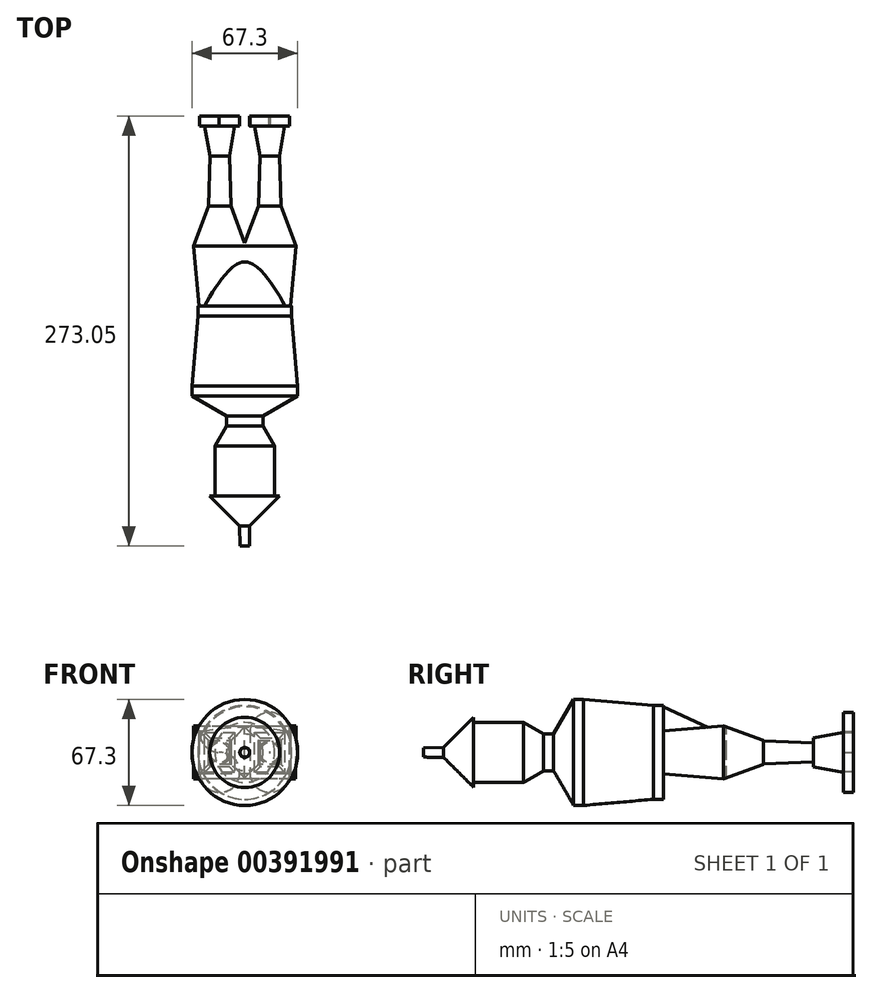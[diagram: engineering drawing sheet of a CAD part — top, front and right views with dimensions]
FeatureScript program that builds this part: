
annotation { "Feature Type Name" : "Feature", "Feature Type Description" : "" }
export const myFeature = defineFeature(function(context is Context, id is Id, definition is map)
    precondition{}
    {
        {
            var Q0;
            Q0=qCreatedBy(makeId("Front.planeOp"),FACE);
            var sketch = newSketch(context, id + "F0", { "sketchPlane" : qUnion([Q0])});
            skLineSegment(sketch, "E0", {"start": v(0, 0) * mm, "end": v(15.88, 0) * mm});
            skCircle(sketch, "E1", {"center": v(15.88, 12.7) * mm, "radius": 12.7 * mm});
            skCircle(sketch, "E2", {"center": v(15.88, -12.69) * mm, "radius": 12.7 * mm});
            skLineSegment(sketch, "E3", {"start": v(28.58, -12.69) * mm, "end": v(28.58, 12.7) * mm});
            skLineSegment(sketch, "E4", {"start": v(15.88, -12.69) * mm, "end": v(15.88, 12.7) * mm});
            skLineSegment(sketch, "E5", {"start": v(3.2, 13.5) * mm, "end": v(3.2, -11.9) * mm});
            skLineSegment(sketch, "E6", {"start": v(0, 0) * mm, "end": v(0, 9.4) * mm});
            skCircle(sketch, "E7.MirrorC", {"center": v(-15.88, -12.69) * mm, "radius": 12.7 * mm});
            skLineSegment(sketch, "E8.MirrorCS", {"start": v(-28.58, -12.69) * mm, "end": v(-28.58, 12.7) * mm});
            skCircle(sketch, "E9.MirrorC", {"center": v(-15.88, 12.7) * mm, "radius": 12.7 * mm});
            skLineSegment(sketch, "E10.MirrorCS", {"start": v(-3.2, 13.5) * mm, "end": v(-3.2, -11.9) * mm});
            skSolve(sketch);
        }
        {
            var Q0;
            {var subQ0=sQuery(id+"F0.wireOp",EDGE,"E5");var subQ1=sQuery(id+"F0.wireOp",EDGE,"E1");var subQ2=makeQuery(id+"F0.imprint","INTERSECT",VERTEX,{"disambiguationData":[OD(0.0)],"derivedFrom":[subQ1,subQ0]});Q0=makeQuery(id+"F0.imprint","IMPRINT",FACE,{"disambiguationData":[TD([[makeQuery(id+"F0.imprint","IMPRINT",EDGE,{"disambiguationData":[TD([[subQ2,-1.0]])],"derivedFrom":subQ1}),1.0]])]});}
            var Q1;
            {var subQ0=sQuery(id+"F0.wireOp",EDGE,"E10.MirrorCS");var subQ1=sQuery(id+"F0.wireOp",EDGE,"E9.MirrorC");var subQ2=makeQuery(id+"F0.imprint","INTERSECT",VERTEX,{"disambiguationData":[OD(0.0)],"derivedFrom":[subQ1,subQ0]});Q1=makeQuery(id+"F0.imprint","IMPRINT",FACE,{"disambiguationData":[TD([[makeQuery(id+"F0.imprint","IMPRINT",EDGE,{"disambiguationData":[TD([[subQ2,-1.0]])],"derivedFrom":subQ1}),-1.0]])]});}
            var Q2;
            {var subQ0=sQuery(id+"F0.wireOp",EDGE,"E5");var subQ1=sQuery(id+"F0.wireOp",EDGE,"E0");var subQ2=makeQuery(id+"F0.imprint","INTERSECT",VERTEX,{"derivedFrom":[subQ1,subQ0]});Q2=makeQuery(id+"F0.imprint","IMPRINT",FACE,{"disambiguationData":[TD([[makeQuery(id+"F0.imprint","IMPRINT",EDGE,{"disambiguationData":[TD([[subQ2,-1.0]])],"derivedFrom":subQ1}),-1.0]])]});}
            var Q3;
            {var subQ0=sQuery(id+"F0.wireOp",EDGE,"E3");Q3=makeQuery(id+"F0.imprint","IMPRINT",FACE,{"disambiguationData":[TD([[makeQuery(id+"F0.imprint","IMPRINT",EDGE,{"derivedFrom":subQ0}),1.0]])]});}
            var Q4;
            {var subQ0=sQuery(id+"F0.wireOp",EDGE,"E10.MirrorCS");var subQ1=sQuery(id+"F0.wireOp",EDGE,"E7.MirrorC");var subQ2=makeQuery(id+"F0.imprint","INTERSECT",VERTEX,{"derivedFrom":[subQ1,subQ0]});Q4=makeQuery(id+"F0.imprint","IMPRINT",FACE,{"disambiguationData":[TD([[makeQuery(id+"F0.imprint","IMPRINT",EDGE,{"disambiguationData":[TD([[subQ2,1.0]])],"derivedFrom":subQ1}),1.0]])]});}
            var Q5;
            {var subQ0=sQuery(id+"F0.wireOp",EDGE,"E5");var subQ1=sQuery(id+"F0.wireOp",EDGE,"E0");var subQ2=makeQuery(id+"F0.imprint","INTERSECT",VERTEX,{"derivedFrom":[subQ1,subQ0]});Q5=makeQuery(id+"F0.imprint","IMPRINT",FACE,{"disambiguationData":[TD([[makeQuery(id+"F0.imprint","IMPRINT",EDGE,{"disambiguationData":[TD([[subQ2,-1.0]])],"derivedFrom":subQ1}),1.0]])]});}
            var Q6;
            {var subQ0=sQuery(id+"F0.wireOp",EDGE,"E2");var subQ6=makeQuery(id+"F0.imprint","INTERSECT",VERTEX,{"derivedFrom":[subQ0,sQuery(id+"F0.wireOp",EDGE,"E3")]});Q6=makeQuery(id+"F0.imprint","IMPRINT",FACE,{"disambiguationData":[TD([[makeQuery(id+"F0.imprint","IMPRINT",EDGE,{"disambiguationData":[TD([[subQ6,-1.0]])],"derivedFrom":subQ0}),1.0]])]});}
            var Q7;
            {var subQ0=sQuery(id+"F0.wireOp",EDGE,"E9.MirrorC");var subQ2=sQuery(id+"F0.wireOp",EDGE,"E7.MirrorC");var subQ3=makeQuery(id+"F0.imprint","INTERSECT",VERTEX,{"disambiguationData":[OD(0.0)],"derivedFrom":[subQ2,subQ0]});Q7=makeQuery(id+"F0.imprint","IMPRINT",FACE,{"disambiguationData":[TD([[makeQuery(id+"F0.imprint","IMPRINT",EDGE,{"disambiguationData":[TD([[subQ3,-1.0]])],"derivedFrom":subQ2}),1.0]])]});}
            var Q8;
            {var subQ2=sQuery(id+"F0.wireOp",EDGE,"E1");var subQ7=makeQuery(id+"F0.imprint","INTERSECT",VERTEX,{"derivedFrom":[subQ2,sQuery(id+"F0.wireOp",EDGE,"E3")]});Q8=makeQuery(id+"F0.imprint","IMPRINT",FACE,{"disambiguationData":[TD([[makeQuery(id+"F0.imprint","IMPRINT",EDGE,{"disambiguationData":[TD([[subQ7,-1.0]])],"derivedFrom":subQ2}),1.0]])]});}
            var Q9;
            {var subQ0=sQuery(id+"F0.wireOp",EDGE,"E7.MirrorC");var subQ1=makeQuery(id+"F0.imprint","INTERSECT",VERTEX,{"derivedFrom":[subQ0,sQuery(id+"F0.wireOp",EDGE,"E8.MirrorCS")]});Q9=makeQuery(id+"F0.imprint","IMPRINT",FACE,{"disambiguationData":[TD([[makeQuery(id+"F0.imprint","IMPRINT",EDGE,{"disambiguationData":[TD([[subQ1,-1.0]])],"derivedFrom":subQ0}),-1.0]])]});}
            var Q10;
            {var subQ0=sQuery(id+"F0.wireOp",EDGE,"E8.MirrorCS");Q10=makeQuery(id+"F0.imprint","IMPRINT",FACE,{"disambiguationData":[TD([[makeQuery(id+"F0.imprint","IMPRINT",EDGE,{"derivedFrom":subQ0}),-1.0]])]});}
            extrude(context, id + "F1", {"entities" : qUnion([Q0, Q1, Q2, Q3, Q4, Q5, Q6, Q7, Q8, Q9, Q10]), "depth" : 6.35 * mm});
        }
        {
            var Q0;
            Q0=makeQuery(id+"F1.opExtrude","CAP_FACE",FACE,{"disambiguationData":[OSD([sQuery(id+"F0.wireOp",EDGE,"E7.MirrorC"),sQuery(id+"F0.wireOp",EDGE,"E8.MirrorCS"),sQuery(id+"F0.wireOp",EDGE,"E9.MirrorC"),sQuery(id+"F0.wireOp",EDGE,"E10.MirrorCS")])],"isStart":false});
            var sketch = newSketch(context, id + "F2", { "sketchPlane" : qUnion([Q0])});
            skLineSegment(sketch, "E11", {"start": v(-15.88, 12.7) * mm, "end": v(-15.88, -12.69) * mm});
            skLineSegment(sketch, "E12", {"start": v(-15.88, -12.69) * mm, "end": v(-6.35, -12.69) * mm});
            skLineSegment(sketch, "E13", {"start": v(-6.35, -12.69) * mm, "end": v(-6.35, 12.71) * mm});
            skLineSegment(sketch, "E14", {"start": v(-6.35, 12.71) * mm, "end": v(-25.4, 12.71) * mm});
            skLineSegment(sketch, "E15", {"start": v(-25.4, 12.71) * mm, "end": v(-25.4, -12.69) * mm});
            skLineSegment(sketch, "E16", {"start": v(-25.4, -12.69) * mm, "end": v(-15.88, -12.69) * mm});
            skLineSegment(sketch, "E17", {"start": v(0, 0.84) * mm, "end": v(0, 11.23) * mm});
            skLineSegment(sketch, "E18.MirrorCS", {"start": v(25.4, -12.69) * mm, "end": v(15.88, -12.69) * mm});
            skLineSegment(sketch, "E19.MirrorCS", {"start": v(15.88, 12.7) * mm, "end": v(15.88, -12.69) * mm});
            skLineSegment(sketch, "E20.MirrorCS", {"start": v(15.88, -12.69) * mm, "end": v(6.35, -12.69) * mm});
            skLineSegment(sketch, "E21.MirrorCS", {"start": v(6.35, 12.71) * mm, "end": v(25.4, 12.71) * mm});
            skLineSegment(sketch, "E22.MirrorCS", {"start": v(25.4, 12.71) * mm, "end": v(25.4, -12.69) * mm});
            skLineSegment(sketch, "E23.MirrorCS", {"start": v(6.35, -12.69) * mm, "end": v(6.35, 12.71) * mm});
            skSolve(sketch);
        }
        {
            var Q0;
            Q0 = qSketchRegion(id + "F2", true);
            extrude(context, id + "F3", {"entities" : qUnion([Q0]), "operationType" : NewBodyOperationType.ADD, "depth" : 19.05 * mm, "hasDraft" : true, "draftAngle" : 10 * degree, "draftPullDirection" : true});
        }
        {
            var Q0;
            Q0=makeQuery(id+"F3.opExtrude","CAP_FACE",FACE,{"disambiguationData":[OSD([sQuery(id+"F2.wireOp",EDGE,"E12"),sQuery(id+"F2.wireOp",EDGE,"E13"),sQuery(id+"F2.wireOp",EDGE,"E14"),sQuery(id+"F2.wireOp",EDGE,"E15"),sQuery(id+"F2.wireOp",EDGE,"E16")])],"isStart":false});
            var sketch = newSketch(context, id + "F4", { "sketchPlane" : qUnion([Q0])});
            skCircle(sketch, "E24", {"center": v(-15.88, 0.01) * mm, "radius": 6.17 * mm});
            skPoint(sketch, "E24.centerSnap0", {"position": v(-15.88, 9.35) * mm});
            skPoint(sketch, "E24.centerSnap1", {"position": v(-22.04, 0.01) * mm});
            skLineSegment(sketch, "E25", {"start": v(0, 0) * mm, "end": v(0, 11.56) * mm});
            skCircle(sketch, "E26.MirrorC", {"center": v(15.88, 0.01) * mm, "radius": 6.17 * mm});
            skSolve(sketch);
        }
        {
            var Q0;
            Q0 = qSketchRegion(id + "F4", true);
            extrude(context, id + "F5", {"entities" : qUnion([Q0]), "operationType" : NewBodyOperationType.ADD, "depth" : 31.75 * mm, "hasDraft" : true, "draftAngle" : 2 * degree});
        }
        {
            var Q0;
            Q0=makeQuery(id+"F5.opExtrude","CAP_FACE",FACE,{"disambiguationData":[OSD([sQuery(id+"F4.wireOp",EDGE,"E24")])],"isStart":false});
            var sketch = newSketch(context, id + "F6", { "sketchPlane" : qUnion([Q0])});
            skLineSegment(sketch, "E27", {"start": v(-8.6, 0) * mm, "end": v(-8.59, 7.62) * mm});
            skLineSegment(sketch, "E28", {"start": v(-8.59, 7.62) * mm, "end": v(-36.98, 7.66) * mm});
            skLineSegment(sketch, "E29", {"start": v(-23.15, 0) * mm, "end": v(-23.16, 7.64) * mm});
            skLineSegment(sketch, "E30", {"start": v(-23.15, 0) * mm, "end": v(-23.14, -7.62) * mm});
            skLineSegment(sketch, "E31", {"start": v(-23.14, -7.62) * mm, "end": v(-8.6, -7.6) * mm});
            skLineSegment(sketch, "E32", {"start": v(-8.6, -7.6) * mm, "end": v(-8.6, 0) * mm});
            skLineSegment(sketch, "E33", {"start": v(0, 0) * mm, "end": v(0, 10.82) * mm});
            skLineSegment(sketch, "E34.MirrorCS", {"start": v(8.6, 0) * mm, "end": v(8.59, 7.62) * mm});
            skLineSegment(sketch, "E35.MirrorCS", {"start": v(8.59, 7.62) * mm, "end": v(36.98, 7.66) * mm});
            skLineSegment(sketch, "E36.MirrorCS", {"start": v(23.15, 0) * mm, "end": v(23.16, 7.64) * mm});
            skLineSegment(sketch, "E37.MirrorCS", {"start": v(23.15, 0) * mm, "end": v(23.14, -7.62) * mm});
            skLineSegment(sketch, "E38.MirrorCS", {"start": v(8.6, -7.6) * mm, "end": v(8.6, 0) * mm});
            skLineSegment(sketch, "E39.MirrorCS", {"start": v(23.14, -7.62) * mm, "end": v(8.6, -7.6) * mm});
            skSolve(sketch);
        }
        {
            var Q0;
            Q0 = qSketchRegion(id + "F6", true);
            extrude(context, id + "F7", {"entities" : qUnion([Q0]), "operationType" : NewBodyOperationType.ADD, "depth" : 25.4 * mm, "hasDraft" : true, "draftAngle" : 20 * degree});
        }
        {
            var Q0;
            Q0=makeQuery(id+"F7.opExtrude","CAP_FACE",FACE,{"disambiguationData":[OSD([sQuery(id+"F6.wireOp",EDGE,"E27"),sQuery(id+"F6.wireOp",EDGE,"E28"),sQuery(id+"F6.wireOp",EDGE,"E29"),sQuery(id+"F6.wireOp",EDGE,"E30"),sQuery(id+"F6.wireOp",EDGE,"E31"),sQuery(id+"F6.wireOp",EDGE,"E32")])],"isStart":false});
            var sketch = newSketch(context, id + "F8", { "sketchPlane" : qUnion([Q0])});
            skLineSegment(sketch, "E40", {"start": v(-32.42, 16.9) * mm, "end": v(32.42, 16.9) * mm});
            skLineSegment(sketch, "E41", {"start": v(32.42, 16.9) * mm, "end": v(32.37, -16.88) * mm});
            skLineSegment(sketch, "E42", {"start": v(32.37, -16.88) * mm, "end": v(-32.37, -16.88) * mm});
            skLineSegment(sketch, "E43", {"start": v(-32.37, -16.88) * mm, "end": v(-32.42, 16.9) * mm});
            skSolve(sketch);
        }
        {
            var Q0;
            Q0 = qSketchRegion(id + "F8", true);
            extrude(context, id + "F9", {"entities" : qUnion([Q0]), "operationType" : NewBodyOperationType.ADD, "depth" : 38.1 * mm, "hasDraft" : true, "draftAngle" : 5 * degree, "draftPullDirection" : true});
        }
        {
            var Q0;
            Q0=makeQuery(id+"F9.opExtrude","CAP_FACE",FACE,{"disambiguationData":[OSD([sQuery(id+"F8.wireOp",EDGE,"E40"),sQuery(id+"F8.wireOp",EDGE,"E41"),sQuery(id+"F8.wireOp",EDGE,"E42"),sQuery(id+"F8.wireOp",EDGE,"E43")])],"isStart":false});
            var sketch = newSketch(context, id + "F10", { "sketchPlane" : qUnion([Q0])});
            skCircle(sketch, "E44", {"center": v(0, 0) * mm, "radius": 29.06 * mm});
            skSolve(sketch);
        }
        {
            var Q0;
            {var subQ0=sQuery(id+"F10.wireOp",EDGE,"E44");var subQ1=makeQuery(id+"F9.opExtrude","CAP_EDGE",EDGE,{"disambiguationData":[OSD([sQuery(id+"F8.wireOp",EDGE,"E43")])],"isStart":false});var subQ2=makeQuery(id+"F10.imprint","INTERSECT",VERTEX,{"disambiguationData":[OD(0.0)],"derivedFrom":[subQ1,subQ0]});Q0=makeQuery(id+"F10.imprint","IMPRINT",FACE,{"disambiguationData":[TD([[makeQuery(id+"F10.imprint","IMPRINT",EDGE,{"disambiguationData":[TD([[subQ2,-1.0]])],"derivedFrom":subQ0}),1.0]])]});}
            var Q1;
            {var subQ0=sQuery(id+"F10.wireOp",EDGE,"E44");var subQ1=makeQuery(id+"F9.opExtrude","CAP_EDGE",EDGE,{"disambiguationData":[OSD([sQuery(id+"F8.wireOp",EDGE,"E42")])],"isStart":false});var subQ2=makeQuery(id+"F10.imprint","INTERSECT",VERTEX,{"disambiguationData":[OD(0.0)],"derivedFrom":[subQ1,subQ0]});Q1=makeQuery(id+"F10.imprint","IMPRINT",FACE,{"disambiguationData":[TD([[makeQuery(id+"F10.imprint","IMPRINT",EDGE,{"disambiguationData":[TD([[subQ2,-1.0]])],"derivedFrom":subQ0}),1.0]])]});}
            var Q2;
            {var subQ0=sQuery(id+"F10.wireOp",EDGE,"E44");var subQ8=makeQuery(id+"F9.opExtrude","CAP_EDGE",EDGE,{"disambiguationData":[OSD([sQuery(id+"F8.wireOp",EDGE,"E40")])],"isStart":false});var subQ10=makeQuery(id+"F10.imprint","INTERSECT",VERTEX,{"disambiguationData":[OD(0.0)],"derivedFrom":[subQ8,subQ0]});Q2=makeQuery(id+"F10.imprint","IMPRINT",FACE,{"disambiguationData":[TD([[makeQuery(id+"F10.imprint","IMPRINT",EDGE,{"disambiguationData":[TD([[subQ10,1.0]])],"derivedFrom":subQ0}),1.0]])]});}
            var Q3;
            {var subQ0=sQuery(id+"F10.wireOp",EDGE,"E44");var subQ1=makeQuery(id+"F9.opExtrude","CAP_EDGE",EDGE,{"disambiguationData":[OSD([sQuery(id+"F8.wireOp",EDGE,"E40")])],"isStart":false});var subQ2=makeQuery(id+"F10.imprint","INTERSECT",VERTEX,{"disambiguationData":[OD(0.0)],"derivedFrom":[subQ1,subQ0]});Q3=makeQuery(id+"F10.imprint","IMPRINT",FACE,{"disambiguationData":[TD([[makeQuery(id+"F10.imprint","IMPRINT",EDGE,{"disambiguationData":[TD([[subQ2,-1.0]])],"derivedFrom":subQ0}),1.0]])]});}
            extrude(context, id + "F11", {"entities" : qUnion([Q0, Q1, Q2, Q3]), "operationType" : NewBodyOperationType.ADD, "oppositeDirection" : true, "depth" : 38.1 * mm, "hasDraft" : true, "draftAngle" : 25 * degree, "draftPullDirection" : true});
        }
        {
            var Q0;
            Q0=makeQuery(id+"F11.boolean.opBoolean","MERGE",FACE,{"derivedFrom":[makeQuery(id+"F9.opExtrude","CAP_FACE",FACE,{"disambiguationData":[OSD([sQuery(id+"F8.wireOp",EDGE,"E40"),sQuery(id+"F8.wireOp",EDGE,"E41"),sQuery(id+"F8.wireOp",EDGE,"E42"),sQuery(id+"F8.wireOp",EDGE,"E43")])],"isStart":false}),makeQuery(id+"F11.opExtrude","CAP_FACE",FACE,{"disambiguationData":[OSD([sQuery(id+"F10.wireOp",EDGE,"E44")])],"isStart":true})]});
            var sketch = newSketch(context, id + "F12", { "sketchPlane" : qUnion([Q0])});
            skCircle(sketch, "E45", {"center": v(0, 0) * mm, "radius": 29.76 * mm});
            skSolve(sketch);
        }
        {
            var Q0;
            Q0 = qSketchRegion(id + "F12", true);
            extrude(context, id + "F13", {"entities" : qUnion([Q0]), "operationType" : NewBodyOperationType.ADD, "depth" : 6.35 * mm});
        }
        {
            var Q0;
            Q0=makeQuery(id+"F13.opExtrude","CAP_FACE",FACE,{"disambiguationData":[OSD([sQuery(id+"F12.wireOp",EDGE,"E45")])],"isStart":false});
            extrude(context, id + "F14", {"entities" : qUnion([Q0]), "operationType" : NewBodyOperationType.ADD, "depth" : 44.45 * mm, "hasDraft" : true, "draftAngle" : 5 * degree});
        }
        {
            var Q0;
            Q0=makeQuery(id+"F14.opExtrude","CAP_FACE",FACE,{"disambiguationData":[OSD([sQuery(id+"F12.wireOp",EDGE,"E45")])],"isStart":false});
            extrude(context, id + "F15", {"entities" : qUnion([Q0]), "operationType" : NewBodyOperationType.ADD, "depth" : 6.35 * mm});
        }
        {
            var Q0;
            Q0=makeQuery(id+"F15.opExtrude","CAP_FACE",FACE,{"disambiguationData":[OSD([sQuery(id+"F12.wireOp",EDGE,"E45")])],"isStart":false});
            extrude(context, id + "F16", {"entities" : qUnion([Q0]), "operationType" : NewBodyOperationType.ADD, "depth" : 12.7 * mm, "hasDraft" : true, "draftAngle" : 60 * degree, "draftPullDirection" : true});
        }
        {
            var Q0;
            Q0=makeQuery(id+"F16.opExtrude","CAP_FACE",FACE,{"disambiguationData":[OSD([sQuery(id+"F12.wireOp",EDGE,"E45")])],"isStart":false});
            extrude(context, id + "F17", {"entities" : qUnion([Q0]), "operationType" : NewBodyOperationType.ADD, "depth" : 6.35 * mm});
        }
        {
            var Q0;
            Q0=makeQuery(id+"F17.opExtrude","CAP_FACE",FACE,{"disambiguationData":[OSD([sQuery(id+"F12.wireOp",EDGE,"E45")])],"isStart":false});
            extrude(context, id + "F18", {"entities" : qUnion([Q0]), "operationType" : NewBodyOperationType.ADD, "depth" : 12.7 * mm, "hasDraft" : true, "draftAngle" : 30 * degree});
        }
        {
            var Q0;
            Q0=makeQuery(id+"F18.opExtrude","CAP_FACE",FACE,{"disambiguationData":[OSD([sQuery(id+"F12.wireOp",EDGE,"E45")])],"isStart":false});
            extrude(context, id + "F19", {"entities" : qUnion([Q0]), "operationType" : NewBodyOperationType.ADD, "depth" : 31.75 * mm});
        }
        {
            var Q0;
            Q0=makeQuery(id+"F19.opExtrude","CAP_FACE",FACE,{"disambiguationData":[OSD([sQuery(id+"F12.wireOp",EDGE,"E45")])],"isStart":false});
            var sketch = newSketch(context, id + "F20", { "sketchPlane" : qUnion([Q0])});
            skCircle(sketch, "E46", {"center": v(0, 0) * mm, "radius": 22.23 * mm});
            skSolve(sketch);
        }
        {
            var Q0;
            Q0 = qSketchRegion(id + "F20", true);
            extrude(context, id + "F21", {"entities" : qUnion([Q0]), "operationType" : NewBodyOperationType.ADD, "depth" : 19.05 * mm, "hasDraft" : true, "draftAngle" : 45 * degree, "draftPullDirection" : true});
        }
        {
            var Q0;
            Q0=makeQuery(id+"F21.opExtrude","CAP_FACE",FACE,{"disambiguationData":[OSD([sQuery(id+"F20.wireOp",EDGE,"E46")])],"isStart":false});
            extrude(context, id + "F22", {"entities" : qUnion([Q0]), "operationType" : NewBodyOperationType.ADD, "depth" : 12.7 * mm, "hasDraft" : true, "draftAngle" : 1 * degree, "draftPullDirection" : true});
        }
    });
